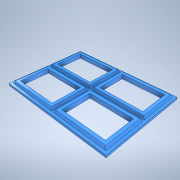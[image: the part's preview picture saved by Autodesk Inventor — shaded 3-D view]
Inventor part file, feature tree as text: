
AUTODESK INVENTOR PART (.ipt)
format: ipt  version: 2021 (Build 250183000, 183)  size: 199,168 bytes
history: native  units: mm
features: extrude x5, sketch x5
ambient origin geometry x8: Origin, YZ Plane, XZ Plane, XY Plane, X Axis, Y Axis, Z Axis, Center Point
bodies: Body1 (feature_tree)
feature tree (10):
  extrude  "Extrusion9"  Depth=105.0mm
  extrude  "Extrusion10"  Depth=6.0mm
  extrude  "Extrusion11"  Depth=140.0mm
  extrude  "Extrusion12"  Depth=3.0mm TaperAngle=0.0deg
  extrude  "Extrusion13"  Depth=50.5mm
  sketch  "Sketch16"  dims[d141=140.0mm d142=105.0mm]
  sketch  "Sketch17"  dims[d143=3.0mm d144=0.0mm]
  sketch  "Sketch18"  dims[d146=20.0mm d148=20.0mm d149=140.0mm d150=105.0mm d151=44.5mm d152=62.0mm d153=5.0mm d154=5.0mm d155=68.0mm d156=50.5mm d157=6.0mm d158=-5.235988mm]
  sketch  "Sketch19"  dims[d159=0.0mm d160=0.0mm d161=140.0mm]
  sketch  "Sketch20"  dims[d162=105.0mm d163=3.0mm d164=0.0mm d166=20.0mm d168=50.5mm d169=20.0mm d171=68.0mm d174=0.0mm d175=0.0mm d82=0.5mm d83=0.872665mm d84=0.5mm d85=0.872665mm d86=0.5mm d87=0.872665mm]
